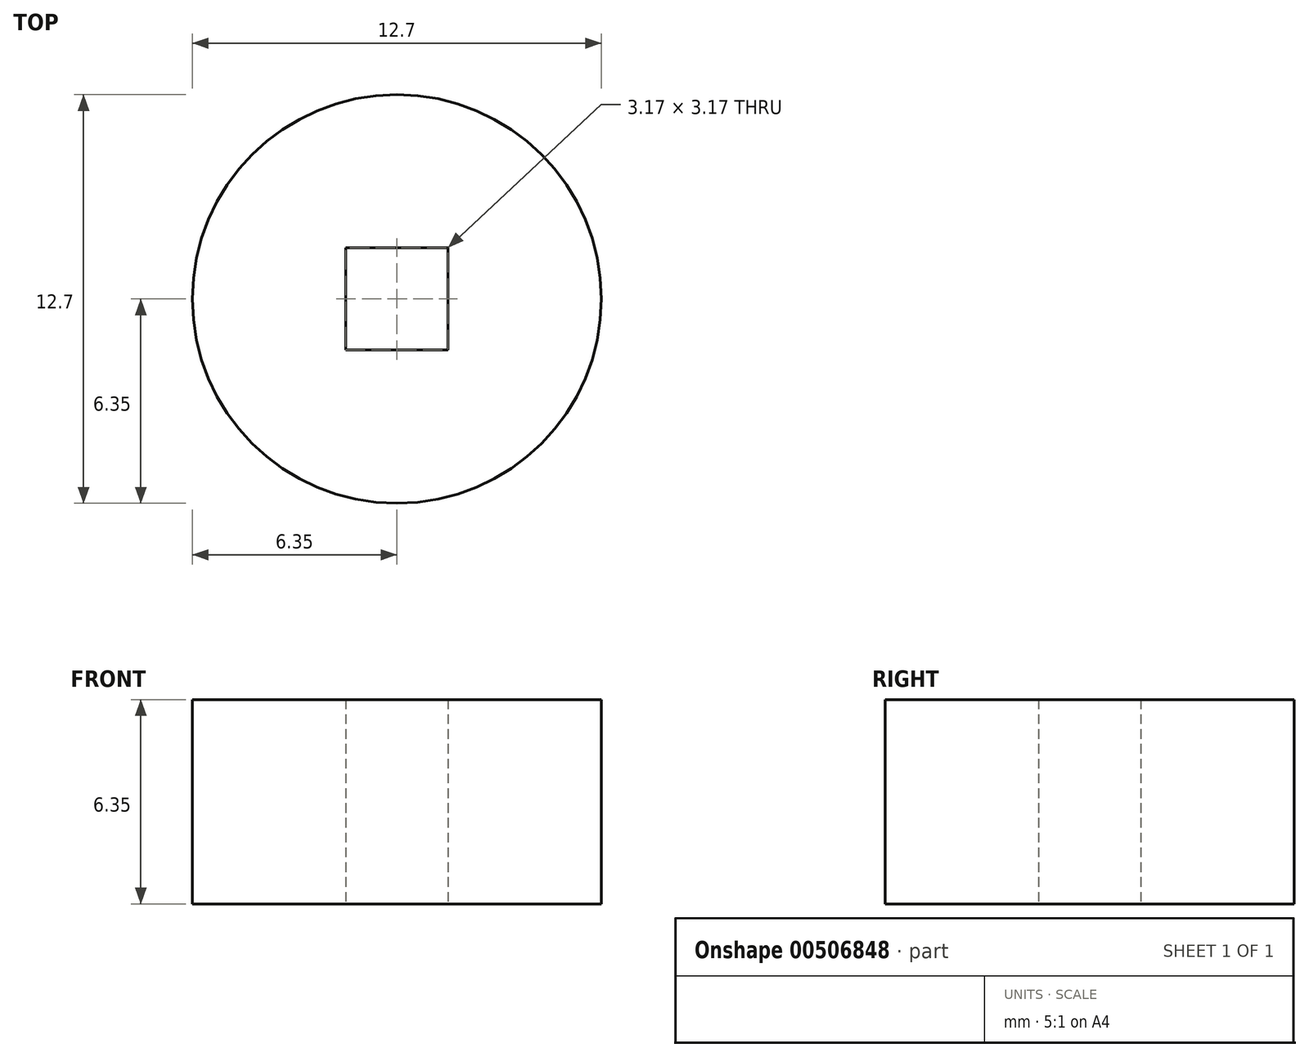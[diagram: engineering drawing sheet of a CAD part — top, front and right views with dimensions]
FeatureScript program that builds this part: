
annotation { "Feature Type Name" : "Feature", "Feature Type Description" : "" }
export const myFeature = defineFeature(function(context is Context, id is Id, definition is map)
    precondition{}
    {
        {
            var Q0;
            Q0=qCreatedBy(makeId("Top.planeOp"),FACE);
            var sketch = newSketch(context, id + "F0", { "sketchPlane" : qUnion([Q0])});
            skCircle(sketch, "E0", {"center": v(0, 0) * mm, "radius": 6.35 * mm});
            skLineSegment(sketch, "E1.bottom", {"start": v(1.59, 1.59) * mm, "end": v(-1.59, 1.59) * mm});
            skLineSegment(sketch, "E1.top", {"start": v(1.59, -1.59) * mm, "end": v(-1.59, -1.59) * mm});
            skLineSegment(sketch, "E1.left", {"start": v(1.59, 1.59) * mm, "end": v(1.59, -1.59) * mm});
            skLineSegment(sketch, "E1.right", {"start": v(-1.59, 1.59) * mm, "end": v(-1.59, -1.59) * mm});
            skSolve(sketch);
        }
        {
            var Q0;
            Q0=makeQuery(id+"F0.imprint","IMPRINT",FACE,{"disambiguationData":[TD([[makeQuery(id+"F0.imprint","IMPRINT",EDGE,{"derivedFrom":sQuery(id+"F0.wireOp",EDGE,"E0")}),1.0]])]});
            extrude(context, id + "F1", {"entities" : qUnion([Q0]), "depth" : 6.35 * mm, "offsetDistance" : 25.4 * mm});
        }
    });
